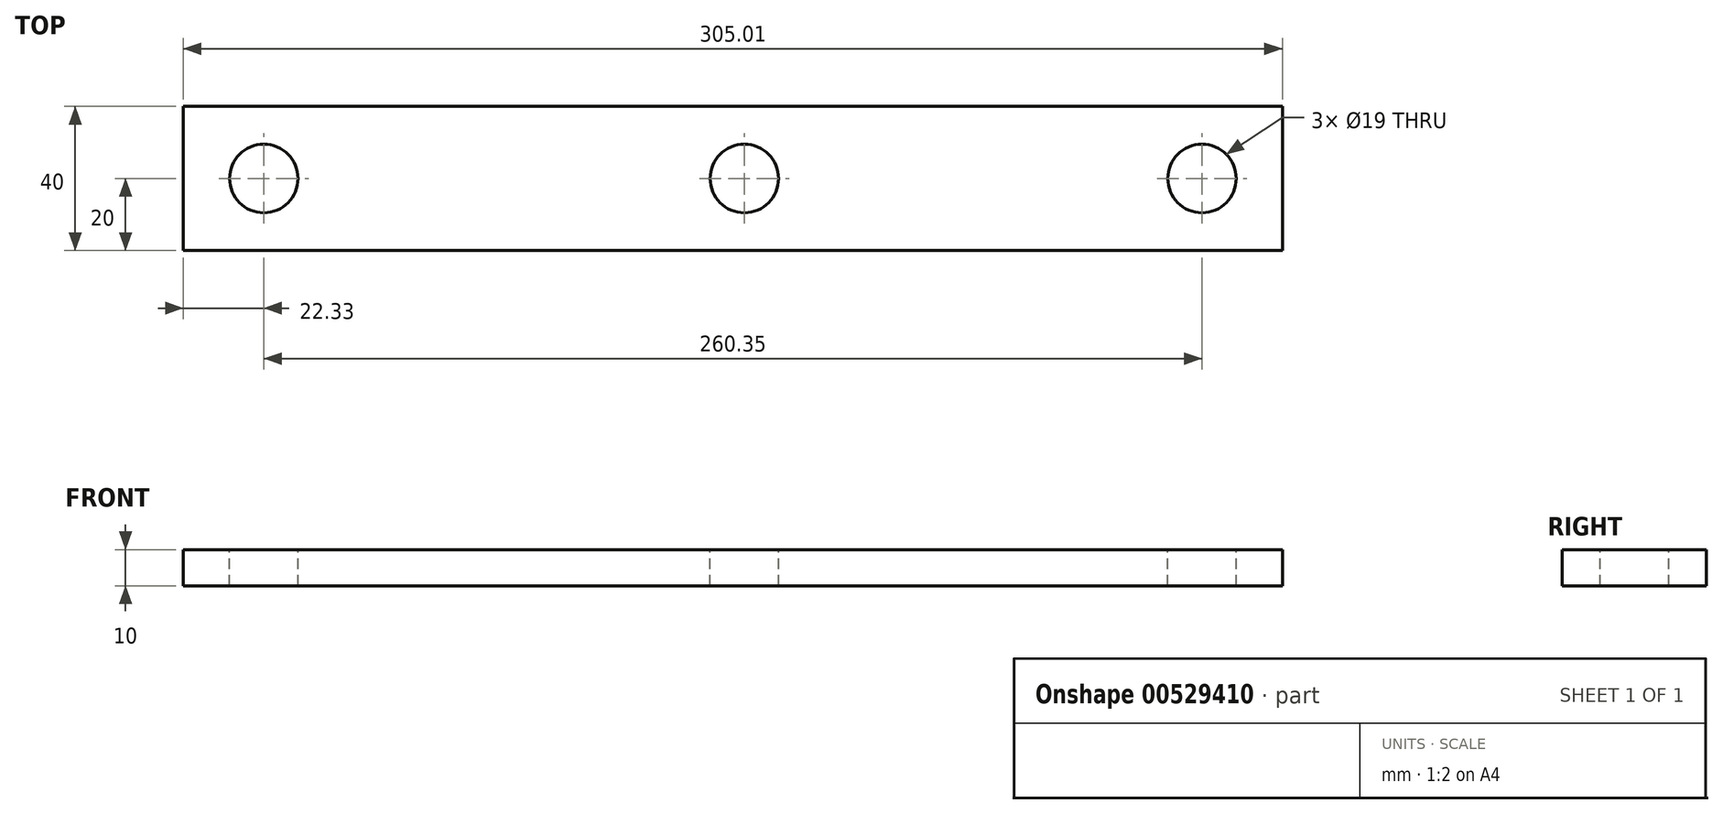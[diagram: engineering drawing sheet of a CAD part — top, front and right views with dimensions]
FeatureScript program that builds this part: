
annotation { "Feature Type Name" : "Feature", "Feature Type Description" : "" }
export const myFeature = defineFeature(function(context is Context, id is Id, definition is map)
    precondition{}
    {
        {
            var Q0;
            Q0=qCreatedBy(makeId("Top.planeOp"),FACE);
            var sketch = newSketch(context, id + "F0", { "sketchPlane" : qUnion([Q0])});
            skPoint(sketch, "E0.middle", {"position": v(0, 0) * mm});
            skLineSegment(sketch, "E1", {"start": v(0, 0) * mm, "end": v(-133.35, 0) * mm, "construction": true});
            skLineSegment(sketch, "E2", {"start": v(0, 0) * mm, "end": v(127, 0) * mm, "construction": true});
            skCircle(sketch, "E3", {"center": v(-133.35, 0) * mm, "radius": 9.5 * mm});
            skCircle(sketch, "E4", {"center": v(0, 0) * mm, "radius": 9.5 * mm});
            skCircle(sketch, "E5", {"center": v(127, 0) * mm, "radius": 9.5 * mm});
            skLineSegment(sketch, "E6", {"start": v(0, 0) * mm, "end": v(0, -20) * mm, "construction": true});
            skLineSegment(sketch, "E7", {"start": v(127, 0) * mm, "end": v(149.32, 0) * mm, "construction": true});
            skLineSegment(sketch, "E8", {"start": v(-133.35, 0) * mm, "end": v(-155.68, 0) * mm, "construction": true});
            skLineSegment(sketch, "E9", {"start": v(0, -20) * mm, "end": v(-155.68, -20) * mm});
            skLineSegment(sketch, "E10.MirrorCS", {"start": v(0, 20) * mm, "end": v(-155.68, 20) * mm});
            skLineSegment(sketch, "E11", {"start": v(0, -20) * mm, "end": v(149.32, -20) * mm});
            skLineSegment(sketch, "E12.MirrorCS", {"start": v(0, 20) * mm, "end": v(149.32, 20) * mm});
            skLineSegment(sketch, "E13", {"start": v(149.32, 20) * mm, "end": v(149.32, -20) * mm});
            skLineSegment(sketch, "E14", {"start": v(-155.68, 20) * mm, "end": v(-155.68, -20) * mm});
            skSolve(sketch);
        }
        {
            var Q0;
            Q0=makeQuery(id+"F0.imprint","IMPRINT",FACE,{"disambiguationData":[TD([[makeQuery(id+"F0.imprint","IMPRINT",EDGE,{"derivedFrom":sQuery(id+"F0.wireOp",EDGE,"E3")}),-1.0]])]});
            extrude(context, id + "F1", {"entities" : qUnion([Q0]), "oppositeDirection" : true, "depth" : 10 * mm, "offsetDistance" : 25 * mm});
        }
    });
